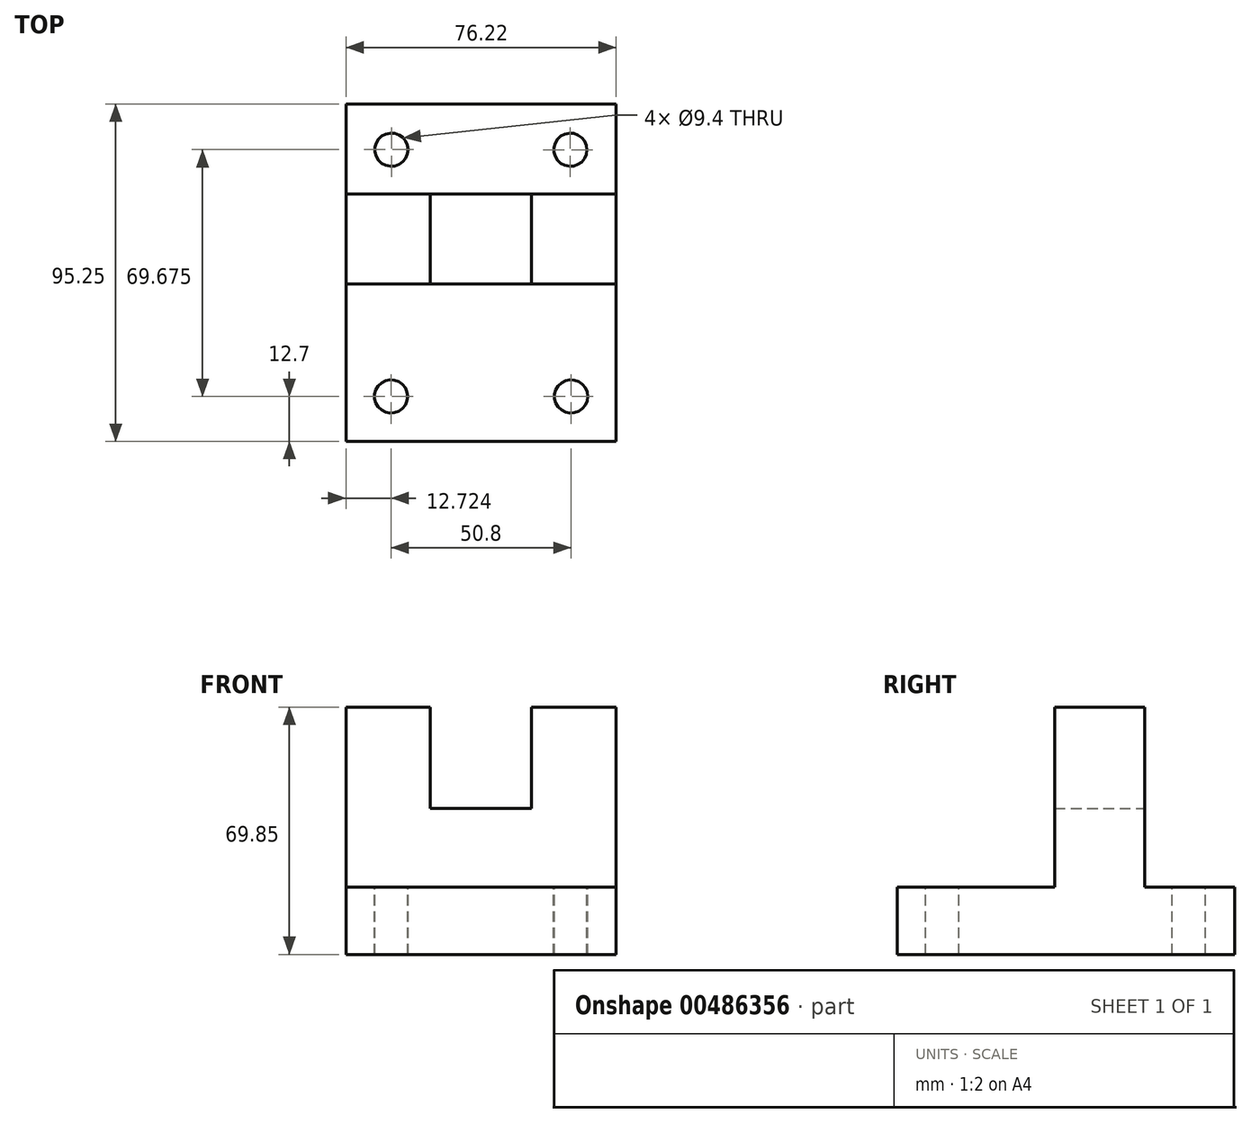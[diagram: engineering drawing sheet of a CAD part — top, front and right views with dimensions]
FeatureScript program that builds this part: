
annotation { "Feature Type Name" : "Feature", "Feature Type Description" : "" }
export const myFeature = defineFeature(function(context is Context, id is Id, definition is map)
    precondition{}
    {
        {
            var Q0;
            Q0=qCreatedBy(makeId("Front.planeOp"),FACE);
            var sketch = newSketch(context, id + "F0", { "sketchPlane" : qUnion([Q0])});
            skLineSegment(sketch, "E0", {"start": v(32.87, -40.7) * mm, "end": v(-43.33, -40.7) * mm});
            skLineSegment(sketch, "E1", {"start": v(32.87, 10.1) * mm, "end": v(32.87, -40.7) * mm});
            skLineSegment(sketch, "E2", {"start": v(32.87, 10.1) * mm, "end": v(9.05, 10.1) * mm});
            skLineSegment(sketch, "E3", {"start": v(9.05, 10.1) * mm, "end": v(9.05, -18.48) * mm});
            skLineSegment(sketch, "E4", {"start": v(9.05, -18.48) * mm, "end": v(-19.53, -18.48) * mm});
            skLineSegment(sketch, "E5", {"start": v(-19.53, -18.48) * mm, "end": v(-19.53, 10.1) * mm});
            skLineSegment(sketch, "E6", {"start": v(-19.53, 10.1) * mm, "end": v(-43.35, 10.1) * mm});
            skLineSegment(sketch, "E7", {"start": v(-43.35, 10.1) * mm, "end": v(-43.33, -40.7) * mm});
            skSolve(sketch);
        }
        {
            var Q0;
            Q0 = qSketchRegion(id + "F0", true);
            extrude(context, id + "F1", {"entities" : qUnion([Q0]), "depth" : 25.4 * mm, "offsetDistance" : 25.4 * mm});
        }
        {
            var Q0;
            Q0=makeQuery(id+"F1.opExtrude","SWEPT_FACE",FACE,{"disambiguationData":[OSD([sQuery(id+"F0.wireOp",EDGE,"E1")])]});
            var sketch = newSketch(context, id + "F2", { "sketchPlane" : qUnion([Q0])});
            skLineSegment(sketch, "E8", {"start": v(-25.4, -40.7) * mm, "end": v(-69.85, -40.7) * mm});
            skLineSegment(sketch, "E9", {"start": v(-69.85, -40.7) * mm, "end": v(-69.85, -59.75) * mm});
            skLineSegment(sketch, "E10", {"start": v(-69.85, -59.75) * mm, "end": v(25.4, -59.75) * mm});
            skLineSegment(sketch, "E11", {"start": v(25.4, -59.75) * mm, "end": v(25.4, -40.7) * mm});
            skLineSegment(sketch, "E12", {"start": v(25.4, -40.7) * mm, "end": v(0, -40.7) * mm});
            skSolve(sketch);
        }
        {
            var Q0;
            Q0 = qSketchRegion(id + "F2", true);
            var Q1;
            Q1=makeQuery(id+"F2.imprint","IMPRINT",FACE,{"disambiguationData":[TD([[makeQuery(id+"F2.imprint","IMPRINT",EDGE,{"derivedFrom":sQuery(id+"F2.wireOp",EDGE,"E8")}),1.0]])]});
            extrude(context, id + "F3", {"entities" : qUnion([Q0, Q1]), "operationType" : NewBodyOperationType.ADD, "oppositeDirection" : true, "depth" : 76.2 * mm, "offsetDistance" : 25.4 * mm});
        }
        {
            var Q0;
            {var subQ1=sQuery(id+"F2.wireOp",EDGE,"E12");var subQ4=sQuery(id+"F2.wireOp",EDGE,"E9");var subQ5=sQuery(id+"F2.wireOp",EDGE,"E8");var subQ6=sQuery(id+"F0.wireOp",EDGE,"E1");var subQ7=sQuery(id+"F0.wireOp",EDGE,"E0");Q0=makeQuery(id+"F3.boolean.opBoolean","SPLIT",FACE,{"disambiguationData":[TD([makeQuery(id+"F3.opExtrude","SWEPT_FACE",FACE,{"disambiguationData":[OSD([subQ4])]})])],"derivedFrom":makeQuery(id+"F3.opExtrude","SWEPT_FACE",FACE,{"disambiguationData":[OSD([subQ7,subQ6,subQ5,subQ1])]})});}
            var sketch = newSketch(context, id + "F4", { "sketchPlane" : qUnion([Q0])});
            skCircle(sketch, "E13", {"center": v(20.17, -57.15) * mm, "radius": 4.7 * mm});
            skCircle(sketch, "E14", {"center": v(-30.63, -57.15) * mm, "radius": 4.7 * mm});
            skCircle(sketch, "E15", {"center": v(19.99, 12.51) * mm, "radius": 4.7 * mm});
            skCircle(sketch, "E16", {"center": v(-30.55, 12.53) * mm, "radius": 4.7 * mm});
            skSolve(sketch);
        }
        {
            var Q0;
            Q0 = qSketchRegion(id + "F4", true);
            extrude(context, id + "F5", {"entities" : qUnion([Q0]), "operationType" : NewBodyOperationType.REMOVE, "oppositeDirection" : true, "depth" : 50.8 * mm, "offsetDistance" : 25.4 * mm});
        }
    });
